# Revit family: BasinMixer-Vitra-OriginSeries-A42583
name_source: partatom
category: Plumbing Fixtures
revit_build: Autodesk Revit 2017 (Build: 20160225_1515(x64)
units: mm (PartAtom-declared; Revit-internal decimal feet)

## family parameters
Cut with Voids When Loaded = No
Host = Face
OmniClass Number = 23.45.55.17
OmniClass Title = Mixing Faucets
Part Type = Normal
Room Calculation Point = No
Round Connector Dimension = Use Diameter
Shared = Yes

## types (4) — shared parameters
BIMobject category = Taps & Mixers
Brand = VitrA
CW Connection = Yes
Connection Diameter (mm) = 10 mm  [stored 0.0328084 ft]
Default Elevation = 850 mm
Design country = Turkey
Flow Rate(L/min. - 3 bar) = 5L/min
HW Connection = Yes
Hot Water Supply (max.) = 80 °C
Hot Water temperature, factory set to = 38 °C
IFC Classification = Sanitary Terminal
Main Material = Brass
Manufacturer = Vitra
Manufacturer name = Vitra
Masterformat 2014 Code = 22 40 00
Masterformat 2014 Description = Plumbing Fixtures
Min. flow pressure of = 0.5 bar
Mounting type = Countertop
NBS Referans Code = 45-35-70/371
NBS Referans Description = Water supply fittings for wash basins and troughs
Nominal Depth (mm) = 170 mm  [stored 0.557743 ft]
Nominal Height (mm) = 135 mm  [stored 0.442913 ft]
Nominal Width (mm) = 420 mm  [stored 1.37795 ft]
Number Of Connections = 2
OmniClass Code = 23.45.55.17
OmniClass Description = Mixing Faucets
Primary Material = <By Category>
Product Type = Basin Mixer
Product certification = https://www.vitraglobal.com
Product data url = https://www.vitra.com.tr
Product family = Origin
Product group = Origin Basin Mixer
Range of Hot Water Supply = 5 - 65 °C
Range of flow pressure = 1 - 5 bar
Technical description = https://www.vitra.com.tr
Test Pressure = 16 bar
URL = https://vitraglobal.com
Uniclass 1.4 Code = L725111
Uniclass 1.4 Description = Mixer taps
Uniclass 2.0 Code = Pr_40_30_96_98
Uniclass 2.0 Description = Washbasin Tap
Uniclass 2015 Code = Pr_40_20_87_98
Uniclass 2015 Name = Washbasin Tap
Uniformat II Code = 22 40 00
Uniformat II Description = Plumbing Fixture
Vent Connection = No
Warranty Period (Year) = 10 Years
Waste Connection = No
Weight Net (kg) = 2.1
Youtube = https://www.youtube.com

## per-type parameters (varying)
| type | Article No. (default) | Coating Material | Color | Description | Model | Product Properties | Product SKU |
| BasinMixer-Vitra-OriginSeries(Matte Black)-A4258336 | A4258336 | Matte Black | Matte Black | Origin Basin Mixer
- 3 tap hole | A4258336 | Green Building Certification
 European Water Label | A4258336 |
| BasinMixer-Vitra-OriginSeries(Nickel)-A4258334 | A4258334 | Nickel | Bright Copper | Origin Basin Mixer - 3 tap hole | A4258334 | Green Building Certification European Water Label | A4258334 |
| BasinMixer-Vitra-OriginSeries(BrightCopper)-A4258326 | A4258326 | BrightCopper | Bright Copper | Origin Basin Mixer
- 3 tap hole | A4258326 | Green Building Certification
 European Water Label | A4258326 |
| BasinMixer-Vitra-OriginSeries(Chrome)-A42583 | A42583 | Chrome | Chrome | Origin Basin Mixer - 3 tap hole | A42583 | Green Building Certification
 European Water Label | A42583 |

note: [stored X ft] marks values corroborated as IEEE doubles in the binary element streams (Revit-internal decimal feet)

## geometry (parser evidence)
native form markers: Sweep x2
no freeform markers — native parametric forms only
